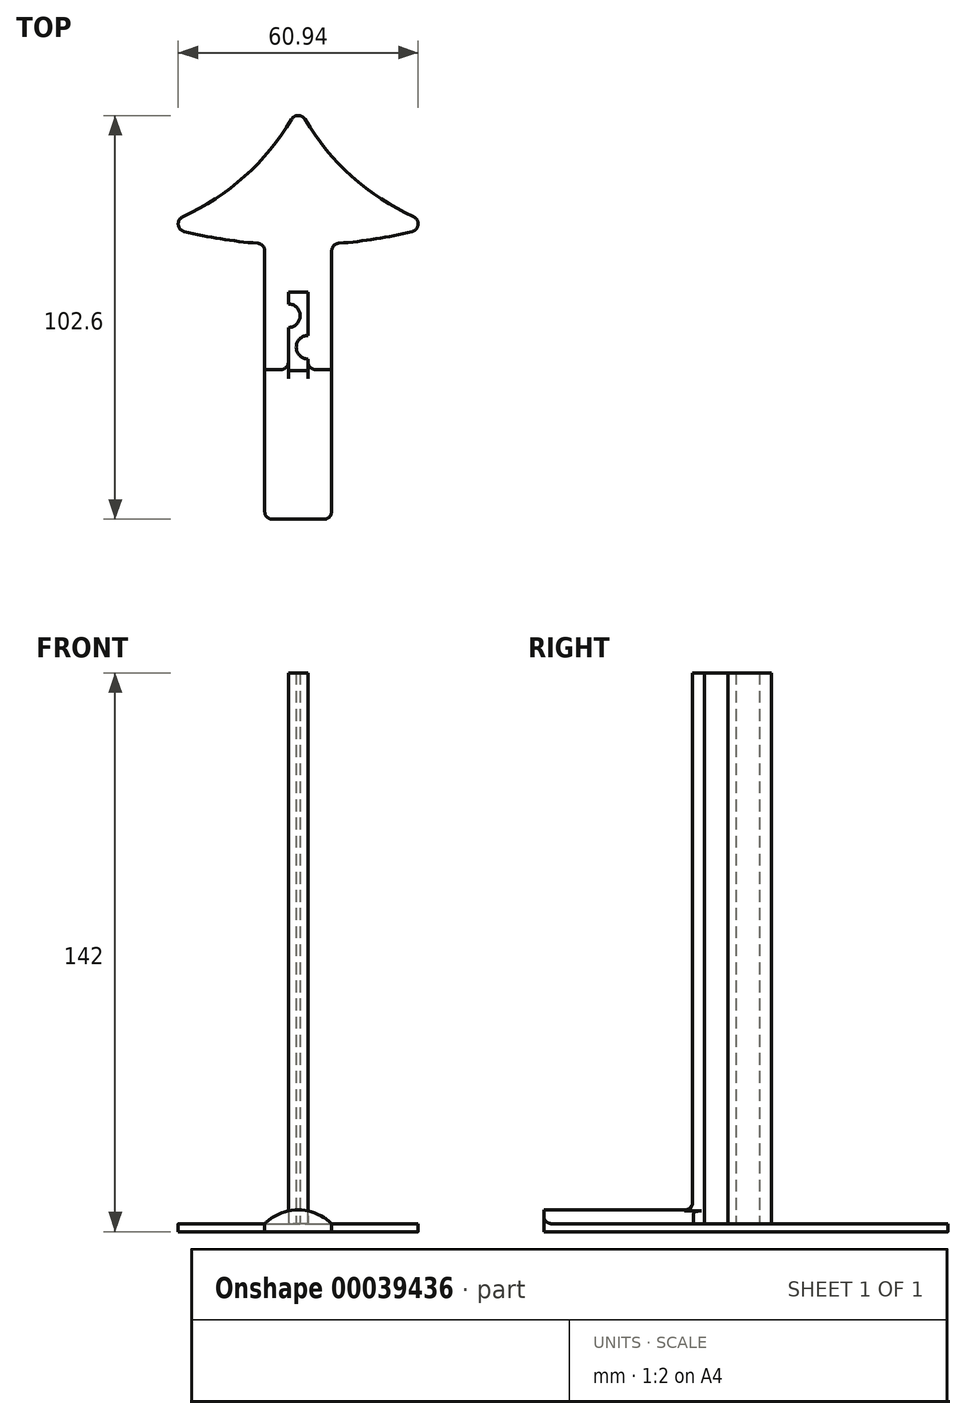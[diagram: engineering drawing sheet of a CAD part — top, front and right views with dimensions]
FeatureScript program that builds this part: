
annotation { "Feature Type Name" : "Feature", "Feature Type Description" : "" }
export const myFeature = defineFeature(function(context is Context, id is Id, definition is map)
    precondition{}
    {
        {
            var Q0;
            Q0=qCreatedBy(makeId("Top.planeOp"),FACE);
            var sketch = newSketch(context, id + "F0", { "sketchPlane" : qUnion([Q0])});
            skLineSegment(sketch, "E0", {"start": v(0, 35) * mm, "end": v(0, -35) * mm, "construction": true});
            skLineSegment(sketch, "E1", {"start": v(-8.5, -34.72) * mm, "end": v(-8.5, -104.72) * mm});
            skLineSegment(sketch, "E2", {"start": v(-8.5, -104.72) * mm, "end": v(0, -104.72) * mm});
            skLineSegment(sketch, "E3.MirrorCS", {"start": v(8.5, -34.72) * mm, "end": v(8.5, -104.72) * mm});
            skLineSegment(sketch, "E4.MirrorCS", {"start": v(8.5, -104.72) * mm, "end": v(0, -104.72) * mm});
            skEllipse(sketch, "E5.0", {"center": v(0, 0) * mm, "majorRadius": 67.5 * mm, "minorRadius": 35 * mm, "majorAxis": v(1, 0), "construction": true});
            skCircle(sketch, "E6.0", {"center": v(-32, 0) * mm, "radius": 17.5 * mm, "construction": true});
            skCircle(sketch, "E7.0", {"center": v(32, 0) * mm, "radius": 17.5 * mm, "construction": true});
            skArc(sketch, "E8", {"start": v(-34.74, -30) * mm, "mid": v(-14.48, -18.35) * mm, "end": v(0, 0) * mm});
            skArc(sketch, "E9.MirrorCS", {"start": v(34.74, -30) * mm, "mid": v(14.48, -18.35) * mm, "end": v(0, 0) * mm});
            skArc(sketch, "E10", {"start": v(-34.74, -30) * mm, "mid": v(-21.76, -33.13) * mm, "end": v(-8.5, -34.72) * mm});
            skArc(sketch, "E11.MirrorCS", {"start": v(34.74, -30) * mm, "mid": v(21.76, -33.13) * mm, "end": v(8.5, -34.72) * mm});
            skSolve(sketch);
        }
        {
            var Q0;
            Q0 = qSketchRegion(id + "F0", true);
            extrude(context, id + "F1", {"entities" : qUnion([Q0]), "depth" : 2 * mm});
        }
        {
            var Q0;
            Q0=makeQuery(id+"F1.opExtrude","CAP_FACE",FACE,{"disambiguationData":[OSD([sQuery(id+"F0.wireOp",EDGE,"7391e9a9-ae98-415e-9696-a7713fd930ae"),sQuery(id+"F0.wireOp",EDGE,"7767e17a-6af5-4bc8-a544-19a58f6916b8"),sQuery(id+"F0.wireOp",EDGE,"E1"),sQuery(id+"F0.wireOp",EDGE,"E2"),sQuery(id+"F0.wireOp",EDGE,"69639bf5-fd83-4191-99ff-23f08a1ee2360.MirrorCS"),sQuery(id+"F0.wireOp",EDGE,"e829f9c4-7dbb-4f23-9f44-d63990e1826a0.MirrorCS"),sQuery(id+"F0.wireOp",EDGE,"E3.MirrorCS"),sQuery(id+"F0.wireOp",EDGE,"E4.MirrorCS")])],"isStart":false});
            var sketch = newSketch(context, id + "F2", { "sketchPlane" : qUnion([Q0])});
            skLineSegment(sketch, "E12", {"start": v(0, 0) * mm, "end": v(0, -57) * mm, "construction": true});
            skLineSegment(sketch, "E13.rect.bottom", {"start": v(2.5, -67) * mm, "end": v(-2.5, -67) * mm});
            skLineSegment(sketch, "E13.rect.top", {"start": v(2.5, -47) * mm, "end": v(-2.5, -47) * mm});
            skLineSegment(sketch, "E13.rect.left", {"start": v(2.5, -67) * mm, "end": v(2.5, -47) * mm, "construction": true});
            skLineSegment(sketch, "E13.rect.right", {"start": v(-2.5, -67) * mm, "end": v(-2.5, -47) * mm, "construction": true});
            skPoint(sketch, "E13.rect.middle", {"position": v(0, -57) * mm});
            skLineSegment(sketch, "E14", {"start": v(-2.5, -47) * mm, "end": v(-2.5, -50) * mm});
            skArc(sketch, "E15", {"start": v(-2.5, -56) * mm, "mid": v(0.5, -53) * mm, "end": v(-2.5, -50) * mm});
            skLineSegment(sketch, "E16", {"start": v(-2.5, -53) * mm, "end": v(-2.5, -47) * mm, "construction": true});
            skLineSegment(sketch, "E17", {"start": v(-2.5, -56) * mm, "end": v(-2.5, -67) * mm});
            skLineSegment(sketch, "E18", {"start": v(2.5, -67) * mm, "end": v(2.5, -64) * mm});
            skArc(sketch, "E19", {"start": v(2.5, -58) * mm, "mid": v(-0.5, -61) * mm, "end": v(2.5, -64) * mm});
            skLineSegment(sketch, "E20", {"start": v(2.5, -58) * mm, "end": v(2.5, -47) * mm});
            skLineSegment(sketch, "E21", {"start": v(2.5, -61) * mm, "end": v(2.5, -57) * mm, "construction": true});
            skSolve(sketch);
        }
        {
            var Q0;
            Q0 = qSketchRegion(id + "F2", true);
            extrude(context, id + "F3", {"entities" : qUnion([Q0]), "operationType" : NewBodyOperationType.ADD, "depth" : 140 * mm});
        }
        {
            var Q0;
            Q0=makeQuery(id+"F1.opExtrude","SWEPT_FACE",FACE,{"disambiguationData":[OSD([sQuery(id+"F0.wireOp",EDGE,"E2"),sQuery(id+"F0.wireOp",EDGE,"E4.MirrorCS")])]});
            var sketch = newSketch(context, id + "F4", { "sketchPlane" : qUnion([Q0])});
            skLineSegment(sketch, "E22", {"start": v(-8.5, 2) * mm, "end": v(8.5, 2) * mm});
            skArc(sketch, "E23", {"start": v(8.5, 2) * mm, "mid": v(0, 5.53) * mm, "end": v(-8.5, 2) * mm});
            skSolve(sketch);
        }
        {
            var Q0;
            Q0 = qSketchRegion(id + "F4", true);
            extrude(context, id + "F5", {"entities" : qUnion([Q0]), "operationType" : NewBodyOperationType.ADD, "oppositeDirection" : true, "depth" : 38 * mm});
        }
        {
            var Q0;
            Q0=makeQuery(id+"F3.opExtrude","CAP_EDGE",EDGE,{"disambiguationData":[OSD([sQuery(id+"F2.wireOp",EDGE,"E20")])],"isStart":true});
            var Q1;
            Q1=makeQuery(id+"F3.opExtrude","CAP_EDGE",EDGE,{"disambiguationData":[OSD([sQuery(id+"F2.wireOp",EDGE,"E14")])],"isStart":true});
            var Q2;
            Q2=makeQuery(id+"F3.opExtrude","CAP_EDGE",EDGE,{"disambiguationData":[OSD([sQuery(id+"F2.wireOp",EDGE,"E13.rect.top")])],"isStart":true});
            var Q3;
            Q3=makeQuery(id+"F1.opExtrude","SWEPT_EDGE",EDGE,{"disambiguationData":[OSD([sQuery(id+"F0.wireOp",EDGE,"E1"),sQuery(id+"F0.wireOp",EDGE,"E10")])]});
            var Q4;
            Q4=makeQuery(id+"F1.opExtrude","SWEPT_EDGE",EDGE,{"disambiguationData":[OSD([sQuery(id+"F0.wireOp",EDGE,"E1"),sQuery(id+"F0.wireOp",EDGE,"E2")])]});
            var Q5;
            Q5=makeQuery(id+"F1.opExtrude","SWEPT_EDGE",EDGE,{"disambiguationData":[OSD([sQuery(id+"F0.wireOp",EDGE,"E3.MirrorCS"),sQuery(id+"F0.wireOp",EDGE,"E4.MirrorCS")])]});
            var Q6;
            Q6=makeQuery(id+"F1.opExtrude","SWEPT_EDGE",EDGE,{"disambiguationData":[OSD([sQuery(id+"F0.wireOp",EDGE,"E3.MirrorCS"),sQuery(id+"F0.wireOp",EDGE,"E11.MirrorCS")])]});
            var Q7;
            Q7=makeQuery(id+"F1.opExtrude","SWEPT_EDGE",EDGE,{"disambiguationData":[OSD([sQuery(id+"F0.wireOp",EDGE,"E9.MirrorCS"),sQuery(id+"F0.wireOp",EDGE,"E11.MirrorCS")])]});
            var Q8;
            Q8=makeQuery(id+"F1.opExtrude","SWEPT_EDGE",EDGE,{"disambiguationData":[OSD([sQuery(id+"F0.wireOp",EDGE,"E8"),sQuery(id+"F0.wireOp",EDGE,"E10")])]});
            var Q9;
            Q9=makeQuery(id+"F1.opExtrude","SWEPT_EDGE",EDGE,{"disambiguationData":[OSD([sQuery(id+"F0.wireOp",EDGE,"E8"),sQuery(id+"F0.wireOp",EDGE,"E9.MirrorCS")])]});
            var Q10;
            Q10=makeQuery(id+"F5.boolean.opBoolean","INTERSECT",EDGE,{"derivedFrom":[makeQuery(id+"F3.opExtrude","SWEPT_FACE",FACE,{"disambiguationData":[OSD([sQuery(id+"F2.wireOp",EDGE,"E18")])]}),makeQuery(id+"F5.opExtrude","CAP_FACE",FACE,{"disambiguationData":[OSD([sQuery(id+"F4.wireOp",EDGE,"E22"),sQuery(id+"F4.wireOp",EDGE,"E23")])],"isStart":false})]});
            var Q11;
            {var subQ0=sQuery(id+"F4.wireOp",EDGE,"E22");var subQ2=sQuery(id+"F0.wireOp",EDGE,"E3.MirrorCS");Q11=makeQuery(id+"F5.boolean.opBoolean","SPLIT",EDGE,{"disambiguationData":[TD([makeQuery(id+"F1.opExtrude","SWEPT_FACE",FACE,{"disambiguationData":[OSD([subQ2])]})])],"derivedFrom":makeQuery(id+"F5.opExtrude","CAP_EDGE",EDGE,{"disambiguationData":[OSD([subQ0])],"isStart":false})});}
            var Q12;
            Q12=makeQuery(id+"F5.boolean.opBoolean","INTERSECT",EDGE,{"derivedFrom":[makeQuery(id+"F3.opExtrude","SWEPT_FACE",FACE,{"disambiguationData":[OSD([sQuery(id+"F2.wireOp",EDGE,"E17")])]}),makeQuery(id+"F5.opExtrude","CAP_FACE",FACE,{"disambiguationData":[OSD([sQuery(id+"F4.wireOp",EDGE,"E22"),sQuery(id+"F4.wireOp",EDGE,"E23")])],"isStart":false})]});
            var Q13;
            {var subQ0=sQuery(id+"F4.wireOp",EDGE,"E22");var subQ2=sQuery(id+"F0.wireOp",EDGE,"E1");Q13=makeQuery(id+"F5.boolean.opBoolean","SPLIT",EDGE,{"disambiguationData":[TD([makeQuery(id+"F1.opExtrude","SWEPT_FACE",FACE,{"disambiguationData":[OSD([subQ2])]})])],"derivedFrom":makeQuery(id+"F5.opExtrude","CAP_EDGE",EDGE,{"disambiguationData":[OSD([subQ0])],"isStart":false})});}
            var Q14;
            Q14=makeQuery(id+"F3.opExtrude","CAP_EDGE",EDGE,{"disambiguationData":[OSD([sQuery(id+"F2.wireOp",EDGE,"E17")])],"isStart":true});
            var Q15;
            Q15=makeQuery(id+"F3.opExtrude","CAP_EDGE",EDGE,{"disambiguationData":[OSD([sQuery(id+"F2.wireOp",EDGE,"E18")])],"isStart":true});
            var Q16;
            Q16=makeQuery(id+"F5.boolean.opBoolean","INTERSECT",EDGE,{"derivedFrom":[makeQuery(id+"F3.opExtrude","SWEPT_FACE",FACE,{"disambiguationData":[OSD([sQuery(id+"F2.wireOp",EDGE,"E13.rect.bottom")])]}),makeQuery(id+"F5.opExtrude","SWEPT_FACE",FACE,{"disambiguationData":[OSD([sQuery(id+"F4.wireOp",EDGE,"E23")])]})]});
            fillet(context, id + "F6", {"entities" : qUnion([Q0, Q1, Q2, Q3, Q4, Q5, Q6, Q7, Q8, Q9, Q10, Q11, Q12, Q13, Q14, Q15, Q16]), "radius" : 2 * mm, "tangentPropagation" : true, "allowEdgeOverflow" : false});
        }
    });
